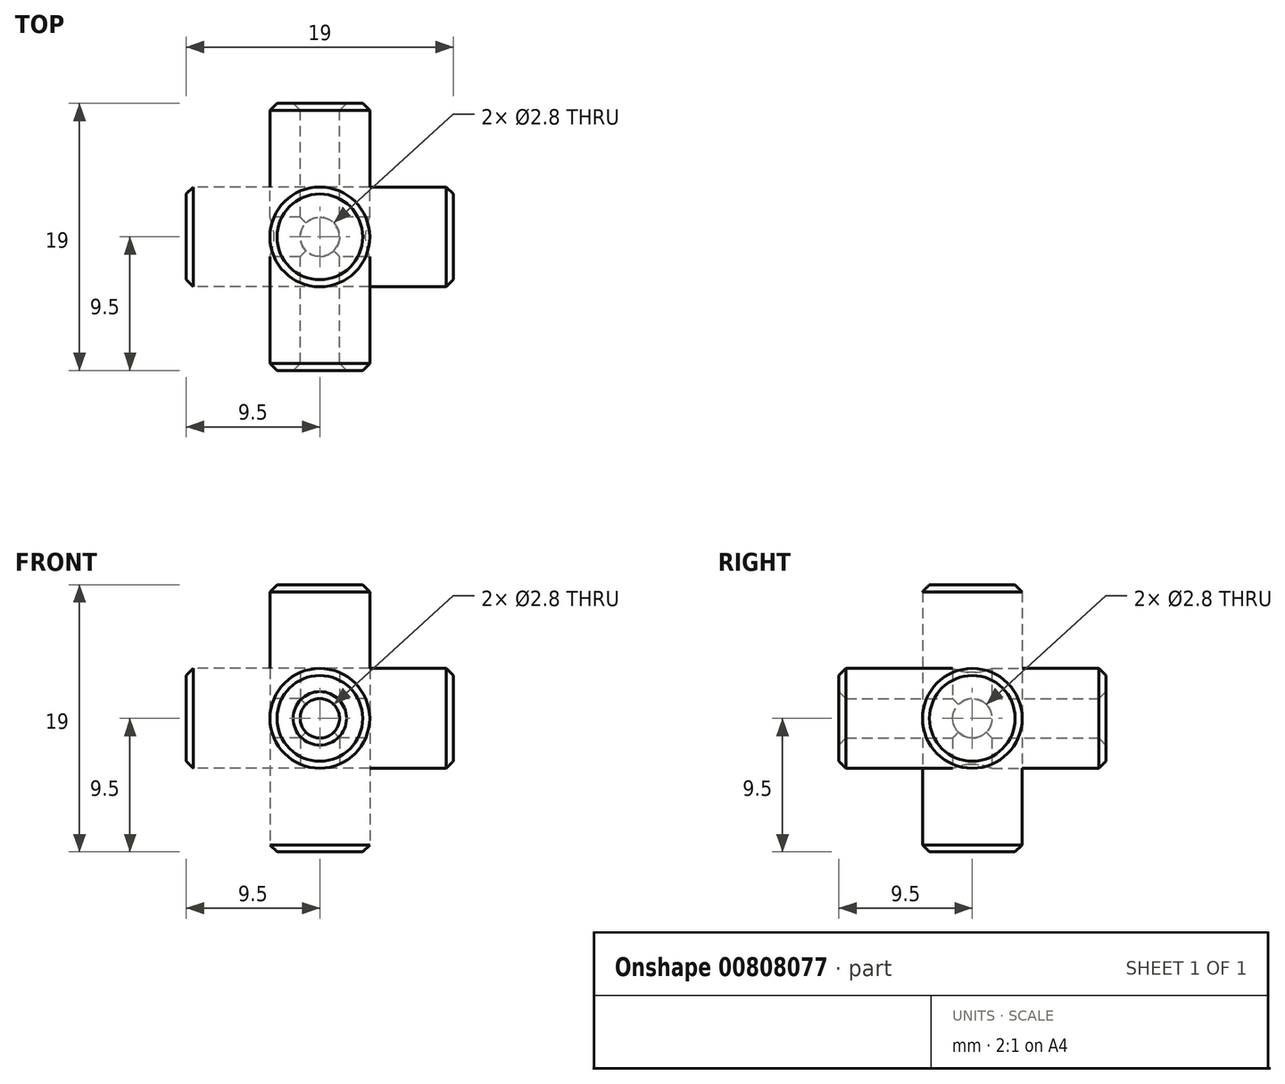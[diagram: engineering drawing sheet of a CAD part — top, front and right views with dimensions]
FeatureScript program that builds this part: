
annotation { "Feature Type Name" : "Feature", "Feature Type Description" : "" }
export const myFeature = defineFeature(function(context is Context, id is Id, definition is map)
    precondition{}
    {
        {
            var Q0;
            Q0=qCreatedBy(makeId("Front.planeOp"),FACE);
            var sketch = newSketch(context, id + "F0", { "sketchPlane" : qUnion([Q0])});
            skCircle(sketch, "E0", {"center": v(0, 0) * mm, "radius": 3.55 * mm});
            skSolve(sketch);
        }
        {
            var Q0;
            Q0=makeQuery(id+"F0.imprint","IMPRINT",FACE,{"disambiguationData":[TD([[makeQuery(id+"F0.imprint","IMPRINT",EDGE,{"derivedFrom":sQuery(id+"F0.wireOp",EDGE,"E0")}),1.0]])]});
            extrude(context, id + "F1", {"entities" : qUnion([Q0]), "endBound" : BoundingType.SYMMETRIC, "depth" : 19 * mm, "offsetDistance" : 25 * mm});
        }
        {
            var Q0;
            Q0=qCreatedBy(makeId("Front.planeOp"),FACE);
            var sketch = newSketch(context, id + "F2", { "sketchPlane" : qUnion([Q0])});
            skCircle(sketch, "E1", {"center": v(0, 0) * mm, "radius": 1.4 * mm});
            skSolve(sketch);
        }
        {
            var Q0;
            Q0 = qSketchRegion(id + "F2", true);
            extrude(context, id + "F3", {"entities" : qUnion([Q0]), "endBound" : BoundingType.SYMMETRIC, "depth" : 20 * mm, "offsetDistance" : 25 * mm});
        }
        {
            var Q0;
            Q0=qCreatedBy(makeId("Front.planeOp"),FACE);
            var sketch = newSketch(context, id + "F4", { "sketchPlane" : qUnion([Q0])});
            skLineSegment(sketch, "E2.bottom", {"start": v(0, 0) * mm, "end": v(10, 0) * mm});
            skLineSegment(sketch, "E2.top", {"start": v(0, 10) * mm, "end": v(10, 10) * mm});
            skLineSegment(sketch, "E2.left", {"start": v(0, 0) * mm, "end": v(0, 10) * mm});
            skLineSegment(sketch, "E2.right", {"start": v(10, 0) * mm, "end": v(10, 10) * mm});
            skSolve(sketch);
        }
        {
            var Q0;
            Q0=makeQuery(id+"F4.imprint","IMPRINT",FACE,{"disambiguationData":[TD([[makeQuery(id+"F4.imprint","IMPRINT",EDGE,{"derivedFrom":sQuery(id+"F4.wireOp",EDGE,"E2.bottom")}),1.0]])]});
            extrude(context, id + "F5", {"entities" : qUnion([Q0]), "depth" : 10 * mm, "offsetDistance" : 25 * mm});
        }
        {
            var Q0;
            Q0=qCreatedBy(makeId("Origin.pointOp"),VERTEX);
            var Q1;
            Q1=makeQuery(id+"F5.opExtrude","CAP_VERTEX",VERTEX,{"disambiguationData":[OSD([sQuery(id+"F4.wireOp",EDGE,"E2.bottom"),sQuery(id+"F4.wireOp",EDGE,"E2.right")])],"isStart":false});
            var Q2;
            Q2=makeQuery(id+"F5.opExtrude","CAP_VERTEX",VERTEX,{"disambiguationData":[OSD([sQuery(id+"F4.wireOp",EDGE,"E2.top"),sQuery(id+"F4.wireOp",EDGE,"E2.right")])],"isStart":false});
            cPlane(context, id + "F6", {"entities" : qUnion([Q0, Q1, Q2]), "cplaneType" : CPlaneType.THREE_POINT, "offset" : 25 * mm, "width" : 150 * mm, "height" : 150 * mm});
        }
        {
            var Q0;
            Q0=qCreatedBy(id+"F6.planeOp",FACE);
            var sketch = newSketch(context, id + "F7", { "sketchPlane" : qUnion([Q0])});
            skLineSegment(sketch, "E3", {"start": v(0, 0) * mm, "end": v(-14.14, 10) * mm});
            skSolve(sketch);
        }
        {
            var Q0;
            Q0=makeQuery(id+"F5.opExtrude","SWEPT_BODY",BODY,{"disambiguationData":[OSD([sQuery(id+"F4.wireOp",EDGE,"E2.bottom"),sQuery(id+"F4.wireOp",EDGE,"E2.top"),sQuery(id+"F4.wireOp",EDGE,"E2.left"),sQuery(id+"F4.wireOp",EDGE,"E2.right")])]});
            deleteBodies(context, id + "F8", {"entities" : qUnion([Q0])});
        }
        {
            var Q0;
            Q0=makeQuery(id+"F1.opExtrude","SWEPT_BODY",BODY,{"disambiguationData":[OSD([sQuery(id+"F0.wireOp",EDGE,"E0")])]});
            var Q1;
            Q1=makeQuery(id+"F3.opExtrude","SWEPT_BODY",BODY,{"disambiguationData":[OSD([sQuery(id+"F2.wireOp",EDGE,"E1")])]});
            var Q2;
            Q2=sQuery(id+"F7.wireOp",EDGE,"E3");
            circularPattern(context, id + "F9", {"entities" : qUnion([Q0, Q1]), "axis" : qUnion([Q2]), "angle" : 360 * degree, "instanceCount" : 3, "equalSpace" : true});
        }
        {
            var Q0;
            Q0=makeQuery(id+"F9.opPattern","COPY",BODY,{"derivedFrom":makeQuery(id+"F3.opExtrude","SWEPT_BODY",BODY,{"disambiguationData":[OSD([sQuery(id+"F2.wireOp",EDGE,"E1")])]}),"instanceName":"2"});
            var Q1;
            Q1=makeQuery(id+"F9.opPattern","COPY",BODY,{"derivedFrom":makeQuery(id+"F3.opExtrude","SWEPT_BODY",BODY,{"disambiguationData":[OSD([sQuery(id+"F2.wireOp",EDGE,"E1")])]}),"instanceName":"1"});
            var Q2;
            Q2=makeQuery(id+"F3.opExtrude","SWEPT_BODY",BODY,{"disambiguationData":[OSD([sQuery(id+"F2.wireOp",EDGE,"E1")])]});
            var Q3;
            Q3=makeQuery(id+"F1.opExtrude","SWEPT_BODY",BODY,{"disambiguationData":[OSD([sQuery(id+"F0.wireOp",EDGE,"E0")])]});
            booleanBodies(context, id + "F10", {"operationType" : BooleanOperationType.SUBTRACTION, "tools" : qUnion([Q0, Q1, Q2]), "targets" : qUnion([Q3])});
        }
        {
            var Q0;
            Q0=makeQuery(id+"F9.opPattern","COPY",FACE,{"derivedFrom":makeQuery(id+"F1.opExtrude","CAP_FACE",FACE,{"disambiguationData":[OSD([sQuery(id+"F0.wireOp",EDGE,"E0")])],"isStart":false}),"instanceName":"2"});
            var Q1;
            Q1=makeQuery(id+"F9.opPattern","COPY",FACE,{"derivedFrom":makeQuery(id+"F1.opExtrude","CAP_FACE",FACE,{"disambiguationData":[OSD([sQuery(id+"F0.wireOp",EDGE,"E0")])],"isStart":true}),"instanceName":"1"});
            var Q2;
            Q2=makeQuery(id+"F1.opExtrude","CAP_FACE",FACE,{"disambiguationData":[OSD([sQuery(id+"F0.wireOp",EDGE,"E0")])],"isStart":false});
            var Q3;
            Q3=makeQuery(id+"F1.opExtrude","CAP_FACE",FACE,{"disambiguationData":[OSD([sQuery(id+"F0.wireOp",EDGE,"E0")])],"isStart":true});
            var Q4;
            Q4=makeQuery(id+"F9.opPattern","COPY",FACE,{"derivedFrom":makeQuery(id+"F1.opExtrude","CAP_FACE",FACE,{"disambiguationData":[OSD([sQuery(id+"F0.wireOp",EDGE,"E0")])],"isStart":true}),"instanceName":"2"});
            var Q5;
            Q5=makeQuery(id+"F9.opPattern","COPY",FACE,{"derivedFrom":makeQuery(id+"F1.opExtrude","CAP_FACE",FACE,{"disambiguationData":[OSD([sQuery(id+"F0.wireOp",EDGE,"E0")])],"isStart":false}),"instanceName":"1"});
            chamfer(context, id + "F11", {"entities" : qUnion([Q0, Q1, Q2, Q3, Q4, Q5]), "width" : 0.5 * mm, "tangentPropagation" : true});
        }
    });
